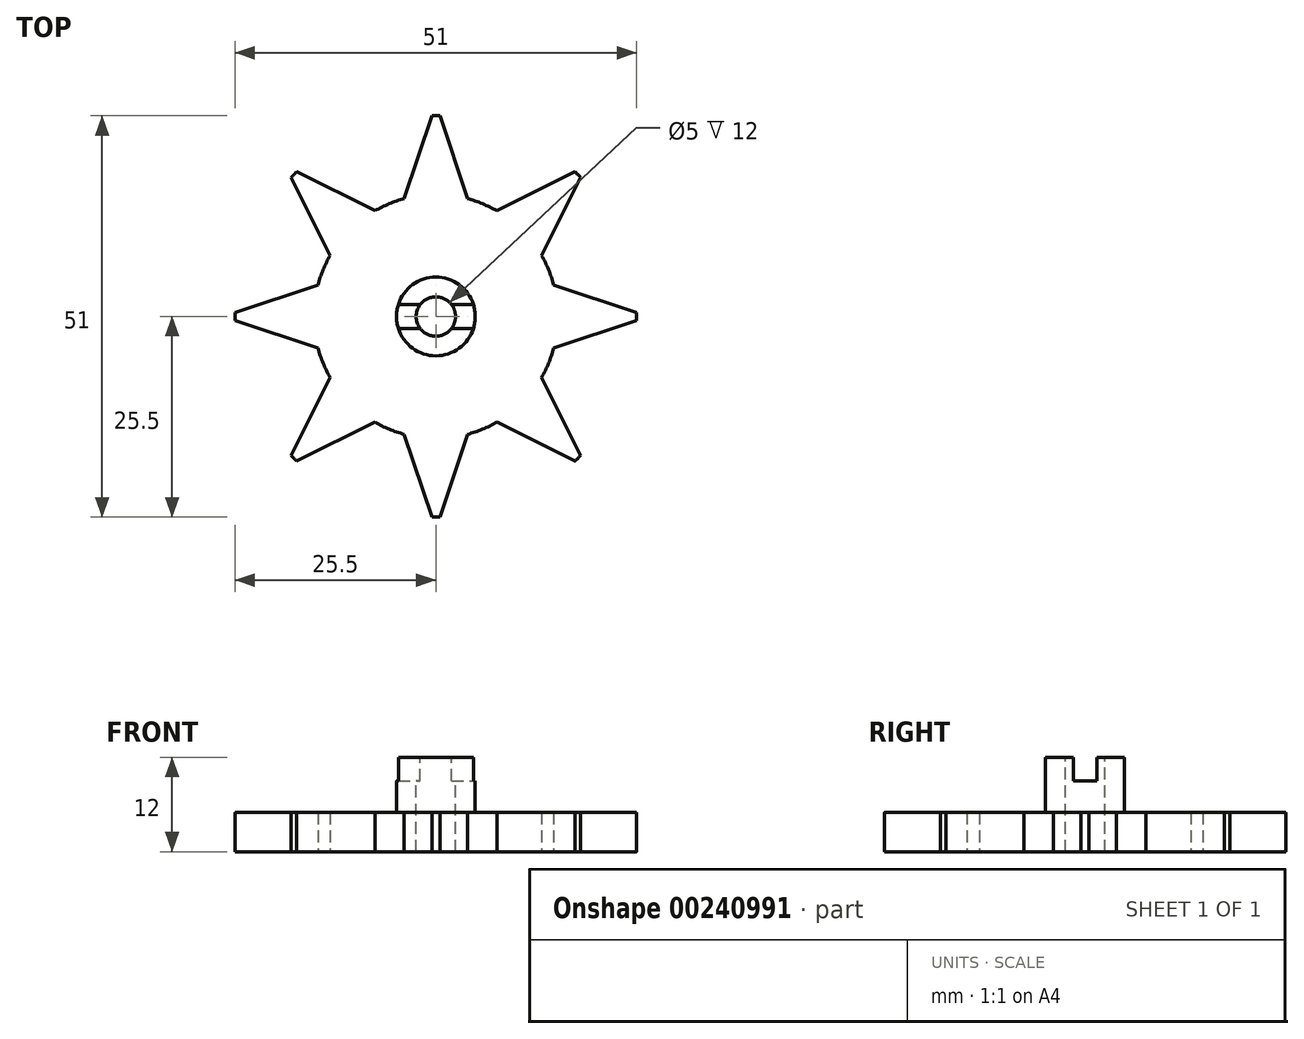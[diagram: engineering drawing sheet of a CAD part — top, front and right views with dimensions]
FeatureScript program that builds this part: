
annotation { "Feature Type Name" : "Feature", "Feature Type Description" : "" }
export const myFeature = defineFeature(function(context is Context, id is Id, definition is map)
    precondition{}
    {
        {
            var Q0;
            Q0=qCreatedBy(makeId("Top.planeOp"),FACE);
            var sketch = newSketch(context, id + "F0", { "sketchPlane" : qUnion([Q0])});
            skArc(sketch, "E0", {"start": v(4.01, 14.97) * mm, "mid": v(0, 15.5) * mm, "end": v(-4.01, 14.97) * mm});
            skArc(sketch, "E1", {"start": v(0.5, 25.5) * mm, "mid": v(0, 25.5) * mm, "end": v(-0.5, 25.5) * mm});
            skLineSegment(sketch, "E2", {"start": v(-0.5, 25.5) * mm, "end": v(-4.01, 14.97) * mm});
            skLineSegment(sketch, "E3", {"start": v(0.5, 25.5) * mm, "end": v(4.01, 14.97) * mm});
            skPoint(sketch, "E4.center.orphan", {"position": v(0, 25.5) * mm});
            skCircle(sketch, "E5", {"center": v(0, 0) * mm, "radius": 15.5 * mm, "construction": true});
            skPoint(sketch, "E6.1.0", {"position": v(-18.03, 18.03) * mm});
            skLineSegment(sketch, "E6.1.1", {"start": v(-17.67, 18.38) * mm, "end": v(-7.75, 13.42) * mm});
            skLineSegment(sketch, "E6.1.2", {"start": v(-18.38, 17.67) * mm, "end": v(-13.42, 7.75) * mm});
            skArc(sketch, "E6.1.3", {"start": v(-7.75, 13.42) * mm, "mid": v(-10.96, 10.96) * mm, "end": v(-13.42, 7.75) * mm});
            skArc(sketch, "E6.1.4", {"start": v(-17.67, 18.38) * mm, "mid": v(-18.03, 18.03) * mm, "end": v(-18.38, 17.67) * mm});
            skPoint(sketch, "E6.2.0", {"position": v(-25.5, 0) * mm});
            skLineSegment(sketch, "E6.2.1", {"start": v(-25.5, 0.5) * mm, "end": v(-14.97, 4.01) * mm});
            skLineSegment(sketch, "E6.2.2", {"start": v(-25.5, -0.5) * mm, "end": v(-14.97, -4.01) * mm});
            skArc(sketch, "E6.2.3", {"start": v(-14.97, 4.01) * mm, "mid": v(-15.5, 0) * mm, "end": v(-14.97, -4.01) * mm});
            skArc(sketch, "E6.2.4", {"start": v(-25.5, 0.5) * mm, "mid": v(-25.5, 0) * mm, "end": v(-25.5, -0.5) * mm});
            skPoint(sketch, "E6.3.0", {"position": v(-18.03, -18.03) * mm});
            skLineSegment(sketch, "E6.3.1", {"start": v(-18.38, -17.67) * mm, "end": v(-13.42, -7.75) * mm});
            skLineSegment(sketch, "E6.3.2", {"start": v(-17.67, -18.38) * mm, "end": v(-7.75, -13.42) * mm});
            skArc(sketch, "E6.3.3", {"start": v(-13.42, -7.75) * mm, "mid": v(-10.96, -10.96) * mm, "end": v(-7.75, -13.42) * mm});
            skArc(sketch, "E6.3.4", {"start": v(-18.38, -17.67) * mm, "mid": v(-18.03, -18.03) * mm, "end": v(-17.67, -18.38) * mm});
            skPoint(sketch, "E6.4.0", {"position": v(0, -25.5) * mm});
            skLineSegment(sketch, "E6.4.1", {"start": v(-0.5, -25.5) * mm, "end": v(-4.01, -14.97) * mm});
            skLineSegment(sketch, "E6.4.2", {"start": v(0.5, -25.5) * mm, "end": v(4.01, -14.97) * mm});
            skArc(sketch, "E6.4.3", {"start": v(-4.01, -14.97) * mm, "mid": v(0, -15.5) * mm, "end": v(4.01, -14.97) * mm});
            skArc(sketch, "E6.4.4", {"start": v(-0.5, -25.5) * mm, "mid": v(0, -25.5) * mm, "end": v(0.5, -25.5) * mm});
            skPoint(sketch, "E6.5.0", {"position": v(18.03, -18.03) * mm});
            skLineSegment(sketch, "E6.5.1", {"start": v(17.67, -18.38) * mm, "end": v(7.75, -13.42) * mm});
            skLineSegment(sketch, "E6.5.2", {"start": v(18.38, -17.67) * mm, "end": v(13.42, -7.75) * mm});
            skArc(sketch, "E6.5.3", {"start": v(7.75, -13.42) * mm, "mid": v(10.96, -10.96) * mm, "end": v(13.42, -7.75) * mm});
            skArc(sketch, "E6.5.4", {"start": v(17.67, -18.38) * mm, "mid": v(18.03, -18.03) * mm, "end": v(18.38, -17.67) * mm});
            skPoint(sketch, "E6.6.0", {"position": v(25.5, 0) * mm});
            skLineSegment(sketch, "E6.6.1", {"start": v(25.5, -0.5) * mm, "end": v(14.97, -4.01) * mm});
            skLineSegment(sketch, "E6.6.2", {"start": v(25.5, 0.5) * mm, "end": v(14.97, 4.01) * mm});
            skArc(sketch, "E6.6.3", {"start": v(14.97, -4.01) * mm, "mid": v(15.5, 0) * mm, "end": v(14.97, 4.01) * mm});
            skArc(sketch, "E6.6.4", {"start": v(25.5, -0.5) * mm, "mid": v(25.5, 0) * mm, "end": v(25.5, 0.5) * mm});
            skPoint(sketch, "E6.7.0", {"position": v(18.03, 18.03) * mm});
            skLineSegment(sketch, "E6.7.1", {"start": v(18.38, 17.67) * mm, "end": v(13.42, 7.75) * mm});
            skLineSegment(sketch, "E6.7.2", {"start": v(17.67, 18.38) * mm, "end": v(7.75, 13.42) * mm});
            skArc(sketch, "E6.7.3", {"start": v(13.42, 7.75) * mm, "mid": v(10.96, 10.96) * mm, "end": v(7.75, 13.42) * mm});
            skArc(sketch, "E6.7.4", {"start": v(18.38, 17.67) * mm, "mid": v(18.03, 18.03) * mm, "end": v(17.67, 18.38) * mm});
            skCircle(sketch, "E7", {"center": v(0, 0) * mm, "radius": 25.5 * mm, "construction": true});
            skCircle(sketch, "E8", {"center": v(0, 0) * mm, "radius": 15.5 * mm});
            skSolve(sketch);
        }
        {
            var Q0;
            Q0 = qSketchRegion(id + "F0", true);
            extrude(context, id + "F1", {"entities" : qUnion([Q0]), "depth" : 5 * mm});
        }
        {
            var Q0;
            Q0=makeQuery(id+"F1.opExtrude","CAP_FACE",FACE,{"disambiguationData":[OSD([sQuery(id+"F0.wireOp",EDGE,"E1"),sQuery(id+"F0.wireOp",EDGE,"E2"),sQuery(id+"F0.wireOp",EDGE,"E3"),sQuery(id+"F0.wireOp",EDGE,"E6.1.1"),sQuery(id+"F0.wireOp",EDGE,"E6.1.2"),sQuery(id+"F0.wireOp",EDGE,"E6.1.4"),sQuery(id+"F0.wireOp",EDGE,"E6.2.1"),sQuery(id+"F0.wireOp",EDGE,"E6.2.2"),sQuery(id+"F0.wireOp",EDGE,"E6.2.4"),sQuery(id+"F0.wireOp",EDGE,"E6.3.1"),sQuery(id+"F0.wireOp",EDGE,"E6.3.2"),sQuery(id+"F0.wireOp",EDGE,"E6.3.4"),sQuery(id+"F0.wireOp",EDGE,"E6.4.1"),sQuery(id+"F0.wireOp",EDGE,"E6.4.2"),sQuery(id+"F0.wireOp",EDGE,"E6.4.4"),sQuery(id+"F0.wireOp",EDGE,"E6.5.1"),sQuery(id+"F0.wireOp",EDGE,"E6.5.2"),sQuery(id+"F0.wireOp",EDGE,"E6.5.4"),sQuery(id+"F0.wireOp",EDGE,"E6.6.1"),sQuery(id+"F0.wireOp",EDGE,"E6.6.2"),sQuery(id+"F0.wireOp",EDGE,"E6.6.4"),sQuery(id+"F0.wireOp",EDGE,"E6.7.1"),sQuery(id+"F0.wireOp",EDGE,"E6.7.2"),sQuery(id+"F0.wireOp",EDGE,"E6.7.4"),sQuery(id+"F0.wireOp",EDGE,"E8")])],"isStart":false});
            var sketch = newSketch(context, id + "F2", { "sketchPlane" : qUnion([Q0])});
            skCircle(sketch, "E9", {"center": v(0, 0) * mm, "radius": 5 * mm});
            skSolve(sketch);
        }
        {
            var Q0;
            Q0 = qSketchRegion(id + "F2", true);
            extrude(context, id + "F3", {"entities" : qUnion([Q0]), "operationType" : NewBodyOperationType.ADD, "depth" : 7 * mm});
        }
        {
            var Q0;
            Q0=makeQuery(id+"F3.opExtrude","CAP_FACE",FACE,{"disambiguationData":[OSD([sQuery(id+"F2.wireOp",EDGE,"E9")])],"isStart":false});
            var sketch = newSketch(context, id + "F4", { "sketchPlane" : qUnion([Q0])});
            skSolve(sketch);
        }
        {
            var Q0;
            Q0=makeQuery(id+"F4.imprint","IMPRINT",FACE,{"disambiguationData":[TD([[makeQuery(id+"F4.imprint","IMPRINT",EDGE,{"derivedFrom":makeQuery(id+"F3.opExtrude","CAP_EDGE",EDGE,{"disambiguationData":[OSD([sQuery(id+"F2.wireOp",EDGE,"E9")])],"isStart":false})}),1.0]])]});
            var sketch = newSketch(context, id + "F5", { "sketchPlane" : qUnion([Q0])});
            skCircle(sketch, "E10", {"center": v(0, 0) * mm, "radius": 2.5 * mm});
            skSolve(sketch);
        }
        {
            var Q0;
            Q0 = qSketchRegion(id + "F5", true);
            extrude(context, id + "F6", {"entities" : qUnion([Q0]), "operationType" : NewBodyOperationType.REMOVE, "endBound" : BoundingType.THROUGH_ALL, "oppositeDirection" : true, "depth" : 25 * mm});
        }
        {
            var Q0;
            Q0=makeQuery(id+"F4.imprint","IMPRINT",FACE,{"disambiguationData":[TD([[makeQuery(id+"F4.imprint","IMPRINT",EDGE,{"derivedFrom":makeQuery(id+"F3.opExtrude","CAP_EDGE",EDGE,{"disambiguationData":[OSD([sQuery(id+"F2.wireOp",EDGE,"E9")])],"isStart":false})}),1.0]])]});
            var sketch = newSketch(context, id + "F7", { "sketchPlane" : qUnion([Q0])});
            skLineSegment(sketch, "E11.bottom", {"start": v(-7.35, 1.5) * mm, "end": v(7.78, 1.5) * mm});
            skLineSegment(sketch, "E11.top", {"start": v(-7.35, -1.5) * mm, "end": v(7.78, -1.5) * mm});
            skLineSegment(sketch, "E11.left", {"start": v(-7.35, 1.5) * mm, "end": v(-7.35, -1.5) * mm});
            skLineSegment(sketch, "E11.right", {"start": v(7.78, 1.5) * mm, "end": v(7.78, -1.5) * mm});
            skSolve(sketch);
        }
        {
            var Q0;
            Q0 = qSketchRegion(id + "F7", true);
            extrude(context, id + "F8", {"entities" : qUnion([Q0]), "operationType" : NewBodyOperationType.REMOVE, "oppositeDirection" : true, "depth" : 3 * mm});
        }
    });
